# Revit family: ACQUA C
name_source: partatom
category: Осветительные приборы
revit_build: Autodesk Revit 2016 (Build: 20150220_1215(x64)
units: mm (PartAtom-declared; Revit-internal decimal feet)

## family parameters
Источник света = Да
Общий = Нет
Основа = Грань
При загрузке вырезать с полостями = Нет
Размер круглого соединителя = Использовать диаметр
Тип детали = Нормальный
Точка расчета площади = Нет

## types (9) — shared parameters
ADSK_Единица измерения = Шт.
ADSK_Завод-изготовитель = ООО МГК Световые технологии
ADSK_Количество фаз = 1
ADSK_Количество фаз числовое = 1
ADSK_Коэффициент мощности = 0.92
ADSK_Наименование = Встраиваемый светильник, создающий прямое диффузное освещение. Корпус светильника изготовлен из алюминия, окрашенного порошковой краской. Оптическая часть закрыта молочным темперированным стеклом
ADSK_Напряжение = 230 В
ADSK_Номинальная мощность = 0 кВт
ADSK_Полная мощность = 0 кВ·А
ADSK_Ток = 0 А
IP Class = IP54
URL = http://www.ltcompany.com
Блок аварийного питания = Нет
Видимая форма излучения при визуализации = Нет
Группа модели = Светильники
Изготовитель = ООО МГК Световые технологии
Класс Защиты = II
Климатическая зона = УХЛ4
Код по классификатору = D5020200
Корпус = Белый металл
Область использования = HoReCa/гостиницы/рестораны/кафе, Конференц залы, Культурно-развлекательные учреждения, Офисно-административные бъекты, ТРЦ, Частные интерьеры
Описание = Встраиваемый светильник, создающий прямое диффузное освещение. Корпус светильника изготовлен из алюминия, окрашенного порошковой краской. Оптическая часть закрыта молочным темперированным стеклом
Плафон = Плафон полупрозрачный
Полная установленная мощность = 0 кВ·А
Светофильтр = 16777215
Смещение цветовой температуры при затухании лампы = <Нет>
Тип ИС = LED
Тип продукции = Светильник
Угол наклона = -90.00°
Файл фотометрической сетки = generic
zero-valued in all types: Отметка по умолчанию

## per-type parameters (varying)
| type | ADSK_Код изделия | ADSK_Масса | ADSK_Энергоэффективность | Излучение по длине прямоугольника | Излучение по ширине прямоугольника | Радиус.кромка | Радиус.стелко | Радиус.теплообменник | Тип ПРА |
| ACQUA C 03 WH 3000K (with driver) | 1596000090 | 0.12 | 41 лм/Вт | 41 мм | 41 мм | 41 мм | 28 мм | 26 мм | Драйвер |
| ACQUA C 03 WH 4000K (with driver) | 1596000160 | 0.12 | 43 лм/Вт | 41 мм | 41 мм | 41 мм | 28 мм | 26 мм | Драйвер |
| ACQUA C 06 WH 3000K (with driver) | 1596000100 | 0.18 | 62 лм/Вт | 55 мм | 55 мм | 55 мм | 42 мм | 40 мм | Драйвер |
| ACQUA C 06 WH 4000K (with driver) | 1596000170 | 0.18 | 69 лм/Вт | 55 мм | 55 мм | 55 мм | 42 мм | 40 мм | Драйвер |
| ACQUA C 12 WH 3000K (with driver) | 1596000110 | 0.24 | 73 лм/Вт | 75 мм | 75 мм | 75 мм | 62 мм | 60 мм | Драйвер |
| ACQUA C 12 WH 4000K (with driver) | 1596000180 | 0.24 | 80 лм/Вт | 75 мм | 75 мм | 75 мм | 62 мм | 60 мм | Драйвер |
| ACQUA C 18 WH 3000K (with driver) | 1596000240 | 0.27 | 82 лм/Вт | 90 мм | 90 мм | 90 мм | 77 мм | 75 мм | Драйвер |
| ACQUA C 18 WH 4000K (with driver) | 1596000190 | 0.27 | 91 лм/Вт | 90 мм | 90 мм | 90 мм | 77 мм | 75 мм | Драйвер |
| ACQUA C 18 WH 4000K HFD | 1596000260 | 0.27 | 91 лм/Вт | 90 мм | 90 мм | 90 мм | 77 мм | 75 мм | Драйвер DALI |
